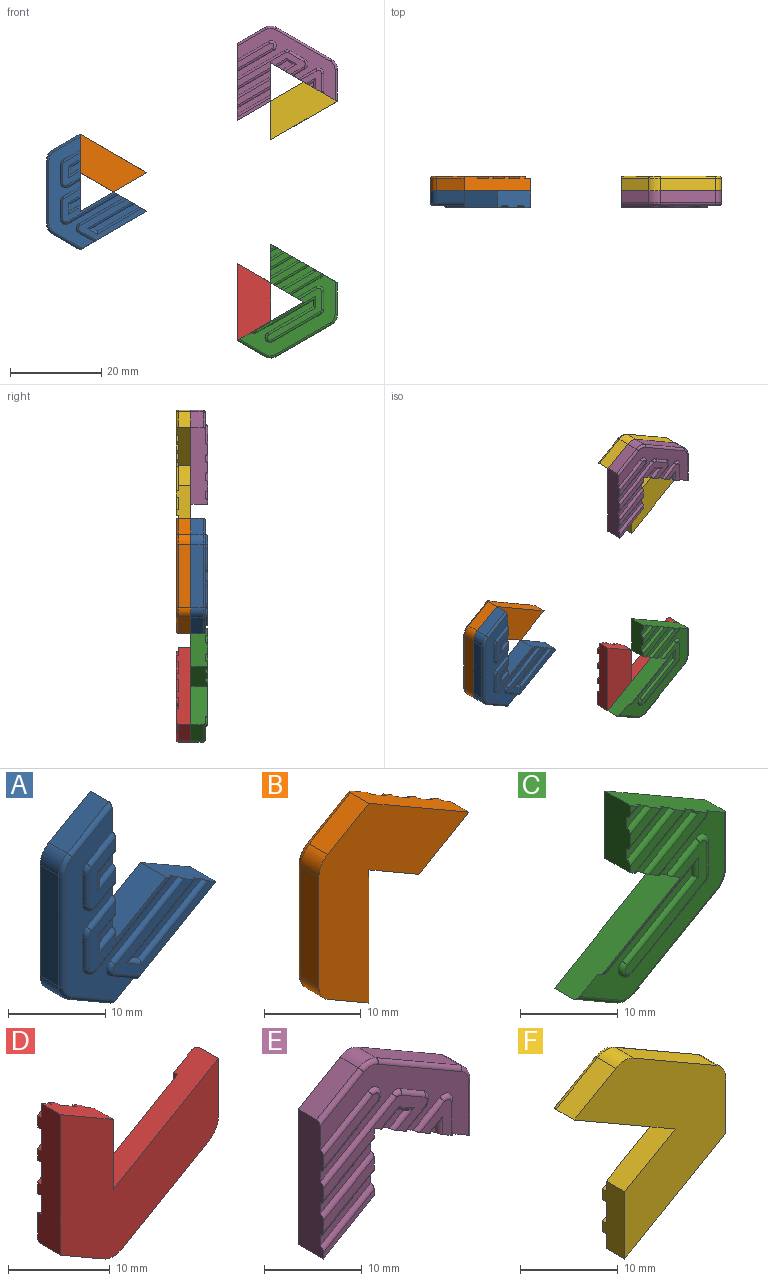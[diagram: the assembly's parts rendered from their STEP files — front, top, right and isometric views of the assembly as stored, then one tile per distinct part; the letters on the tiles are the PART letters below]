
ASSEMBLY  parts=6 mates=14
PART A: 44 faces, bbox 22.1x3.7x25.5 mm
  f0: plane 2.58x2.05mm, normal (0,-1,0), area 2.9mm2, adj f9,f41,f42,f43
  f1: plane 24.46x16.39mm, normal (0,-1,0), area 98.9mm2, adj f6,f7,f9,f17,f18,f19,f20,f21
  f2: plane 2.58x2.05mm, normal (0,-1,0), area 2.9mm2, adj f9,f38,f39,f40
  f3: plane 10.5x6.06mm, normal (0,-1,0), area 12.9mm2, adj f7,f35,f36,f37
  f4: cylinder r=2.54mm len=2.68mm, axis (0,1,0), area 7.1mm2, adj f5,f12,f13,f28
  f5: plane 6.04x3.49mm, normal (-0.5,0,-0.87), area 18.7mm2, adj f4,f6,f13,f27
  f6: plane 14.62x8.44mm, normal (0.5,0,-0.87), area 60.2mm2, adj f1,f5,f7,f13,f14,f27,f32
  f7: plane 7.31x4.22mm, normal (0.5,0,0.87), area 29.4mm2, adj f1,f3,f6,f8,f13,f14,f15,f21
  f8: plane 7.31x4.22mm, normal (-0.5,0,0.87), area 31mm2, adj f7,f9,f13,f15
  f9: plane 16.89x3.68mm, normal (1,0,0), area 57.7mm2, adj f0,f1,f2,f8,f10,f13,f15,f16
  f10: plane 6.04x3.49mm, normal (-0.5,0,0.87), area 18.7mm2, adj f9,f11,f13,f31
  f11: cylinder r=2.54mm len=2.68mm, axis (0,1,0), area 7.1mm2, adj f10,f12,f13,f30
  f12: plane 13.95x2.68mm, normal (-1,0,0), area 37.3mm2, adj f4,f11,f13,f29
  f13: plane 25.33x21.94mm, normal (0,1,0), area 246.3mm2, adj f4,f5,f6,f7,f8,f9,f10,f11
  f14: plane 14.97x9mm, normal (0,-1,0), area 32.7mm2, adj f6,f7,f32,f33,f34,f35,f36,f37
  f15: plane 11.68x7.18mm, normal (0,-1,0), area 18.9mm2, adj f7,f8,f9,f17,f18,f19,f20,f21
  f16: plane 7.18x3.8mm, normal (0,-1,0), area 13.9mm2, adj f9,f22,f23,f24,f25,f26,f41,f42
  f17: cylinder r=0.5mm len=3.99mm, axis (0.87,0,0.5), area 3.3mm2, adj f1,f9,f15,f18
  f18: torus R=0.63mm, axis (0,-1,0), area 0.8mm2, adj f1,f15,f17,f19
  f19: cylinder r=0.5mm len=4mm, axis (0,0,1), area 3.1mm2, adj f1,f15,f18,f20
  f20: torus R=0.63mm, axis (0,-1,0), area 1.6mm2, adj f1,f15,f19,f21
  f21: cylinder r=0.5mm len=11.24mm, axis (-0.87,0,-0.5), area 9.9mm2, adj f1,f7,f15,f20
  f22: cylinder r=0.5mm len=3.99mm, axis (0.87,0,0.5), area 3.3mm2, adj f1,f9,f16,f23
  f23: torus R=0.63mm, axis (0,-1,0), area 0.8mm2, adj f1,f16,f22,f24
  f24: cylinder r=0.5mm len=4mm, axis (0,0,1), area 3.1mm2, adj f1,f16,f23,f25
  f25: torus R=0.63mm, axis (0,-1,0), area 1.6mm2, adj f1,f16,f24,f26
  f26: cylinder r=0.5mm len=3.11mm, axis (-0.87,0,-0.5), area 2.5mm2, adj f1,f9,f16,f25
  f27: cylinder r=0.5mm len=6.54mm, axis (-0.87,0,0.5), area 5.6mm2, adj f1,f5,f6,f28
  f28: torus R=2.04mm, axis (0,-1,0), area 1.9mm2, adj f1,f4,f27,f29
  f29: cylinder r=0.5mm len=13.95mm, axis (0,0,1), area 11mm2, adj f1,f12,f28,f30
  f30: torus R=2.04mm, axis (0,-1,0), area 1.9mm2, adj f1,f11,f29,f31
  f31: cylinder r=0.5mm len=6.29mm, axis (0.87,0,0.5), area 5.4mm2, adj f1,f9,f10,f30
  f32: cylinder r=0.5mm len=3.86mm, axis (-0.87,0,0.5), area 3.1mm2, adj f1,f6,f14,f33
  f33: torus R=0.63mm, axis (0,-1,0), area 1.6mm2, adj f1,f14,f32,f34
  f34: cylinder r=0.5mm len=10.36mm, axis (0.87,0,0.5), area 9mm2, adj f1,f7,f14,f33
  f35: cylinder r=0.5mm len=10.3mm, axis (-0.87,0,-0.5), area 8.6mm2, adj f3,f7,f14,f37
  f36: cylinder r=0.5mm len=10.04mm, axis (0.87,0,0.5), area 8.6mm2, adj f3,f7,f14,f37
  f37: cylinder r=0.5mm len=2.46mm, axis (0.87,0,-0.5), area 1.4mm2, adj f3,f14,f35,f36
  f38: cylinder r=0.5mm len=3.05mm, axis (0.87,0,0.5), area 2mm2, adj f2,f9,f15,f39
  f39: cylinder r=0.5mm len=2.55mm, axis (0,0,-1), area 1.4mm2, adj f2,f15,f38,f40
  f40: cylinder r=0.5mm len=2.8mm, axis (-0.87,0,-0.5), area 2mm2, adj f2,f9,f15,f39
  f41: cylinder r=0.5mm len=2.8mm, axis (-0.87,0,-0.5), area 2mm2, adj f0,f9,f16,f43
  f42: cylinder r=0.5mm len=3.05mm, axis (0.87,0,0.5), area 2mm2, adj f0,f9,f16,f43
  f43: cylinder r=0.5mm len=2.55mm, axis (0,0,-1), area 1.4mm2, adj f0,f16,f41,f42
PART B: 48 faces, bbox 22.1x3.2x25.5 mm
  f0: plane 7.31x4.22mm, normal (0.5,0,-0.87), area 22.6mm2, adj f6,f13,f14,f38
  f1: plane 24.46x9.86mm, normal (0,1,0), area 86.3mm2, adj f6,f12,f16,f17,f18,f22,f23,f24
  f2: plane 8.52x4.92mm, normal (0,1,0), area 10.2mm2, adj f6,f13,f29,f41
  f3: plane 8.56x5.64mm, normal (0,1,0), area 11.1mm2, adj f6,f27,f31,f32
  f4: plane 8.52x4.92mm, normal (0,1,0), area 10.2mm2, adj f6,f13,f39,f42
  f5: plane 2.58x2.05mm, normal (0,1,0), area 2.9mm2, adj f12,f15,f20,f21
  f6: plane 14.62x8.44mm, normal (0.5,0,0.87), area 49mm2, adj f0,f1,f2,f3,f4,f7,f14,f28
  f7: plane 6.04x3.49mm, normal (-0.5,0,0.87), area 18.7mm2, adj f6,f8,f14,f47
  f8: cylinder r=2.54mm len=2.68mm, axis (0,-1,0), area 7.1mm2, adj f7,f9,f14,f46
  f9: plane 13.95x2.68mm, normal (-1,0,0), area 37.3mm2, adj f8,f10,f14,f45
  f10: cylinder r=2.54mm len=2.68mm, axis (0,-1,0), area 7.1mm2, adj f9,f11,f14,f44
  f11: plane 6.04x3.49mm, normal (-0.5,0,-0.87), area 18.7mm2, adj f10,f12,f14,f43
  f12: plane 16.89x3.18mm, normal (1,0,0), area 49mm2, adj f1,f5,f11,f13,f14,f19,f20,f21
  f13: plane 7.31x4.22mm, normal (-0.5,0,-0.87), area 24mm2, adj f0,f2,f4,f12,f14,f28,f29,f38
  f14: plane 25.33x21.94mm, normal (0,-1,0), area 246.3mm2, adj f0,f6,f7,f8,f9,f10,f11,f12
  f15: plane 1.39x0.5mm, normal (-1,0,0), area 0.7mm2, adj f5,f19,f20,f21
  f16: cylinder r=1.13mm len=0.98mm, axis (0,1,0), area 0.6mm2, adj f1,f17,f19,f22
  f17: plane 4x0.5mm, normal (1,0,0), area 2mm2, adj f1,f16,f18,f19
  f18: cylinder r=1.13mm len=1.69mm, axis (0,1,0), area 1.2mm2, adj f1,f17,f19,f23
  f19: plane 8.26x4.3mm, normal (0,1,0), area 24.6mm2, adj f12,f15,f16,f17,f18,f20,f21,f22
  f20: plane 2.05x1.18mm, normal (0.5,0,-0.87), area 1.2mm2, adj f5,f12,f15,f19
  f21: plane 2.05x1.18mm, normal (-0.5,0,0.87), area 1.2mm2, adj f5,f12,f15,f19
  f22: plane 3.74x2.16mm, normal (0.5,0,-0.87), area 2.2mm2, adj f1,f12,f16,f19
  f23: plane 2.61x1.51mm, normal (-0.5,0,0.87), area 1.5mm2, adj f1,f12,f18,f19
  f24: cylinder r=1.13mm len=0.98mm, axis (0,1,0), area 0.6mm2, adj f1,f25,f28,f33
  f25: plane 4x0.5mm, normal (1,0,0), area 2mm2, adj f1,f24,f26,f28
  f26: cylinder r=1.13mm len=1.69mm, axis (0,1,0), area 1.2mm2, adj f1,f25,f28,f30
  f27: plane 1.39x0.5mm, normal (-1,0,0), area 0.7mm2, adj f3,f28,f31,f32
  f28: plane 13.07x10.02mm, normal (0,1,0), area 54.2mm2, adj f6,f12,f13,f24,f25,f26,f27,f29
  f29: plane 7.32x4.22mm, normal (-0.5,0,0.87), area 4.2mm2, adj f2,f6,f13,f28
  f30: plane 2.61x1.51mm, normal (-0.5,0,0.87), area 1.5mm2, adj f1,f12,f26,f28
  f31: plane 8.56x4.94mm, normal (0.5,0,-0.87), area 4.9mm2, adj f3,f6,f27,f28
  f32: plane 7.35x4.24mm, normal (-0.5,0,0.87), area 4.2mm2, adj f3,f6,f27,f28
  f33: plane 6.79x3.92mm, normal (0.5,0,-0.87), area 3.9mm2, adj f1,f6,f24,f28
  f34: cylinder r=1.13mm len=1.95mm, axis (0,1,0), area 1.2mm2, adj f1,f35,f36,f37
  f35: plane 2.28x0.85mm, normal (0,1,0), area 1.4mm2, adj f12,f34,f36,f37
  f36: plane 0.5x0.28mm, normal (0.5,0,-0.87), area 0.2mm2, adj f1,f12,f34,f35
  f37: plane 0.5x0.28mm, normal (0.5,0,0.87), area 0.2mm2, adj f1,f12,f34,f35
  f38: plane 8.51x4.91mm, normal (0,1,0), area 10.1mm2, adj f0,f6,f13,f39
  f39: plane 7.31x4.22mm, normal (0.5,0,-0.87), area 4.2mm2, adj f4,f6,f13,f38
  f40: plane 9.57x5.52mm, normal (0,1,0), area 19mm2, adj f6,f13,f41,f42
  f41: plane 7.31x4.22mm, normal (0.5,0,-0.87), area 4.2mm2, adj f2,f6,f13,f40
  f42: plane 7.32x4.22mm, normal (-0.5,0,0.87), area 4.2mm2, adj f4,f6,f13,f40
  f43: cylinder r=0.5mm len=6.29mm, axis (-0.87,0,0.5), area 5.4mm2, adj f1,f11,f12,f44
  f44: torus R=2.04mm, axis (0,-1,0), area 1.9mm2, adj f1,f10,f43,f45
  f45: cylinder r=0.5mm len=13.95mm, axis (0,0,1), area 11mm2, adj f1,f9,f44,f46
  f46: torus R=2.04mm, axis (0,-1,0), area 1.9mm2, adj f1,f8,f45,f47
  f47: cylinder r=0.5mm len=6.54mm, axis (0.87,0,0.5), area 5.6mm2, adj f1,f6,f7,f46
PART C: 45 faces, bbox 22.1x3.7x25.1 mm
  f0: plane 2.66x2.23mm, normal (0,-1,0), area 2.9mm2, adj f10,f11,f38,f39
  f1: plane 6.12x4.23mm, normal (0,-1,0), area 7.7mm2, adj f10,f11,f40,f42
  f2: plane 8.3x4.92mm, normal (0,-1,0), area 10.2mm2, adj f10,f12,f41,f43,f44
  f3: plane 20.94x17.76mm, normal (0,-1,0), area 104.9mm2, adj f4,f10,f12,f19,f20,f21,f22,f23
  f4: plane 14.62x8.44mm, normal (-0.5,0,0.87), area 60.2mm2, adj f3,f5,f12,f13,f14,f19,f20,f31
  f5: plane 6.04x3.49mm, normal (-0.5,0,-0.87), area 18.7mm2, adj f4,f6,f13,f31
  f6: cylinder r=2.54mm len=2.68mm, axis (0,1,0), area 7.1mm2, adj f5,f7,f13,f32
  f7: plane 12.08x6.98mm, normal (0.5,0,-0.87), area 37.3mm2, adj f6,f8,f13,f33
  f8: cylinder r=2.54mm len=2.68mm, axis (0,1,0), area 7.1mm2, adj f7,f9,f13,f34
  f9: plane 6.98x2.68mm, normal (1,0,0), area 18.7mm2, adj f8,f10,f13,f35
  f10: plane 14.62x8.44mm, normal (0.5,0,0.87), area 57.8mm2, adj f0,f1,f2,f3,f9,f11,f13,f15
  f11: plane 8.44x3.68mm, normal (-1,0,0), area 29.4mm2, adj f0,f1,f10,f12,f13,f16,f17,f18
  f12: plane 7.31x4.22mm, normal (-0.5,0,-0.87), area 29.4mm2, adj f2,f3,f4,f11,f13,f14,f15,f16
  f13: plane 24.94x21.94mm, normal (0,1,0), area 246.3mm2, adj f4,f5,f6,f7,f8,f9,f10,f11
  f14: plane 14.82x11.36mm, normal (0,-1,0), area 28.2mm2, adj f4,f12,f20,f21,f22,f23,f24,f25
  f15: plane 8.34x5.07mm, normal (0,-1,0), area 10.6mm2, adj f10,f12,f36,f37,f43,f44
  f16: plane 7.87x4.95mm, normal (0,-1,0), area 10.3mm2, adj f10,f11,f12,f41,f42
  f17: plane 4.42x3.27mm, normal (0,-1,0), area 5.5mm2, adj f10,f11,f39,f40
  f18: plane 1.1x0.96mm, normal (0,-1,0), area 0.5mm2, adj f10,f11,f38
  f19: cylinder r=0.5mm len=0.42mm, axis (-0.87,0,0.5), area 0mm2, adj f3,f4,f20
  f20: torus R=0.63mm, axis (0,-1,0), area 0.8mm2, adj f3,f4,f14,f19,f21
  f21: cylinder r=0.5mm len=13.35mm, axis (-0.87,0,-0.5), area 11.5mm2, adj f3,f14,f20,f22
  f22: cylinder r=0.5mm len=2.55mm, axis (0,0,1), area 1.4mm2, adj f3,f14,f21,f23
  f23: cylinder r=0.5mm len=10.53mm, axis (0.87,0,0.5), area 9.2mm2, adj f3,f14,f22,f24
  f24: torus R=0.63mm, axis (0,-1,0), area 1.9mm2, adj f3,f14,f23,f25
  f25: cylinder r=0.5mm len=0.69mm, axis (-0.97,0,-0.26), area 0.4mm2, adj f3,f14,f24,f26
  f26: cylinder r=0.5mm len=10.84mm, axis (-0.87,0,-0.5), area 9.6mm2, adj f3,f14,f25,f27
  f27: torus R=0.63mm, axis (0,-1,0), area 0.8mm2, adj f3,f14,f26,f28
  f28: cylinder r=0.5mm len=4mm, axis (0,0,-1), area 3.1mm2, adj f3,f14,f27,f29
  f29: torus R=0.63mm, axis (0,-1,0), area 1.6mm2, adj f3,f14,f28,f30
  f30: cylinder r=0.5mm len=4.44mm, axis (0.87,0,0.5), area 3.7mm2, adj f3,f12,f14,f29
  f31: cylinder r=0.5mm len=6.29mm, axis (-0.87,0,0.5), area 5.4mm2, adj f3,f4,f5,f32
  f32: torus R=2.04mm, axis (0,-1,0), area 1.9mm2, adj f3,f6,f31,f33
  f33: cylinder r=0.5mm len=12.33mm, axis (-0.87,0,-0.5), area 11mm2, adj f3,f7,f32,f34
  f34: torus R=2.04mm, axis (0,-1,0), area 1.9mm2, adj f3,f8,f33,f35
  f35: cylinder r=0.5mm len=7.27mm, axis (0,0,-1), area 5.6mm2, adj f3,f9,f10,f34
  f36: cylinder r=0.5mm len=7.03mm, axis (-0.87,0,-0.5), area 6mm2, adj f3,f12,f15,f37
  f37: torus R=0.63mm, axis (0,-1,0), area 0.6mm2, adj f3,f10,f15,f36
  f38: cylinder r=0.5mm len=1.71mm, axis (-0.87,0,-0.5), area 1.2mm2, adj f0,f10,f11,f18
  f39: cylinder r=0.5mm len=3.41mm, axis (0.87,0,0.5), area 2.6mm2, adj f0,f10,f11,f17
  f40: cylinder r=0.5mm len=5.17mm, axis (-0.87,0,-0.5), area 4.3mm2, adj f1,f10,f11,f17
  f41: cylinder r=0.5mm len=7.81mm, axis (-0.87,0,-0.5), area 6.6mm2, adj f2,f10,f12,f16
  f42: cylinder r=0.5mm len=6.87mm, axis (0.87,0,0.5), area 5.7mm2, adj f1,f10,f11,f16
  f43: cylinder r=0.5mm len=0.54mm, axis (0,0,1), area 0.2mm2, adj f2,f10,f15,f44
  f44: cylinder r=0.5mm len=7.59mm, axis (0.87,0,0.5), area 6.4mm2, adj f2,f12,f15,f43
PART D: 44 faces, bbox 22.4x3.2x20.9 mm
  f0: plane 14.62x8.44mm, normal (-0.5,0,0.87), area 46.9mm2, adj f5,f12,f13,f14,f25,f30,f43
  f1: plane 7.31x5.62mm, normal (0,1,0), area 10.2mm2, adj f5,f7,f27,f33
  f2: plane 2.66x2.23mm, normal (0,1,0), area 2.9mm2, adj f6,f7,f36,f38
  f3: plane 6.12x4.23mm, normal (0,1,0), area 7.7mm2, adj f6,f7,f32,f35
  f4: plane 4.77x3.45mm, normal (0,1,0), area 5.8mm2, adj f5,f15,f28,f29
  f5: plane 8.44x3.18mm, normal (1,0,0), area 24mm2, adj f0,f1,f4,f6,f14,f25,f27,f28
  f6: plane 7.31x4.22mm, normal (0.5,0,0.87), area 24mm2, adj f2,f3,f5,f7,f14,f31,f32,f34
  f7: plane 16.89x3.18mm, normal (-1,0,0), area 49mm2, adj f1,f2,f3,f6,f8,f13,f14,f25
  f8: plane 6.04x3.49mm, normal (-0.5,0,-0.87), area 18.7mm2, adj f7,f9,f14,f39
  f9: cylinder r=2.54mm len=2.68mm, axis (0,-1,0), area 7.1mm2, adj f8,f10,f14,f40
  f10: plane 12.08x6.98mm, normal (0.5,0,-0.87), area 37.3mm2, adj f9,f11,f14,f41
  f11: cylinder r=2.54mm len=2.68mm, axis (0,-1,0), area 7.1mm2, adj f10,f12,f14,f42
  f12: plane 6.98x2.68mm, normal (1,0,0), area 18.7mm2, adj f0,f11,f14,f43
  f13: plane 21.44x15.7mm, normal (0,1,0), area 95.2mm2, adj f0,f7,f16,f17,f18,f19,f20,f21
  f14: plane 21.94x20.72mm, normal (0,-1,0), area 246.3mm2, adj f0,f5,f6,f7,f8,f9,f10,f11
  f15: plane 1.21x0.69mm, normal (-0.5,0,-0.87), area 0.7mm2, adj f4,f25,f28,f29
  f16: cylinder r=1.13mm len=1.13mm, axis (0,1,0), area 0.6mm2, adj f13,f17,f25,f26
  f17: plane 12.35x7.13mm, normal (-0.5,0,0.87), area 7.1mm2, adj f13,f16,f18,f25
  f18: plane 1.39x0.5mm, normal (1,0,0), area 0.7mm2, adj f13,f17,f19,f25
  f19: plane 10.03x5.79mm, normal (0.5,0,-0.87), area 5.8mm2, adj f13,f18,f20,f25
  f20: cylinder r=1.13mm len=2.1mm, axis (0,1,0), area 1.5mm2, adj f13,f19,f21,f25
  f21: plane 0.56x0.5mm, normal (-0.26,0,0.97), area 0.3mm2, adj f13,f20,f22,f25
  f22: plane 10.59x6.11mm, normal (-0.5,0,0.87), area 6.1mm2, adj f13,f21,f23,f25
  f23: cylinder r=1.13mm len=0.98mm, axis (0,1,0), area 0.6mm2, adj f13,f22,f24,f25
  f24: plane 4x0.5mm, normal (-1,0,0), area 2mm2, adj f13,f23,f25,f30
  f25: plane 18.93x11.36mm, normal (0,1,0), area 78.9mm2, adj f0,f5,f7,f15,f16,f17,f18,f19
  f26: plane 3.19x1.83mm, normal (0.5,0,0.87), area 1.8mm2, adj f7,f13,f16,f25
  f27: plane 7.31x4.22mm, normal (0.5,0,-0.87), area 4.2mm2, adj f1,f5,f7,f25
  f28: plane 3.56x2.05mm, normal (0.5,0,-0.87), area 2.1mm2, adj f4,f5,f15,f25
  f29: plane 4.77x2.75mm, normal (-0.5,0,0.87), area 2.8mm2, adj f4,f5,f15,f25
  f30: cylinder r=1.13mm len=0.5mm, axis (0,1,0), area 0.1mm2, adj f0,f13,f24,f25
  f31: plane 7.31x6.14mm, normal (0,1,0), area 18.2mm2, adj f5,f6,f7,f32,f33
  f32: plane 6.12x3.53mm, normal (0.5,0,-0.87), area 3.5mm2, adj f3,f6,f7,f31
  f33: plane 7.31x4.22mm, normal (-0.5,0,0.87), area 4.2mm2, adj f1,f5,f7,f31
  f34: plane 4.92x4.14mm, normal (0,1,0), area 9.9mm2, adj f6,f7,f35,f36
  f35: plane 4.92x2.84mm, normal (-0.5,0,0.87), area 2.8mm2, adj f3,f6,f7,f34
  f36: plane 2.66x1.53mm, normal (0.5,0,-0.87), area 1.5mm2, adj f2,f6,f7,f34
  f37: plane 1.68x1.45mm, normal (0,1,0), area 1.2mm2, adj f6,f7,f38
  f38: plane 1.45x0.84mm, normal (-0.5,0,0.87), area 0.8mm2, adj f2,f6,f7,f37
  f39: cylinder r=0.5mm len=6.54mm, axis (-0.87,0,0.5), area 5.6mm2, adj f7,f8,f13,f40
  f40: torus R=2.04mm, axis (0,-1,0), area 1.9mm2, adj f9,f13,f39,f41
  f41: cylinder r=0.5mm len=12.33mm, axis (-0.87,0,-0.5), area 11mm2, adj f10,f13,f40,f42
  f42: torus R=2.04mm, axis (0,-1,0), area 1.9mm2, adj f11,f13,f41,f43
  f43: cylinder r=0.5mm len=6.98mm, axis (0,0,-1), area 5.4mm2, adj f0,f12,f13,f42
PART E: 46 faces, bbox 22.4x3.7x20.9 mm
  f0: plane 7.31x5.61mm, normal (0,-1,0), area 10.2mm2, adj f5,f12,f43,f45
  f1: plane 3.32x1.92mm, normal (0,-1,0), area 2.9mm2, adj f6,f40,f41,f42
  f2: plane 7.31x5.61mm, normal (0,-1,0), area 10.2mm2, adj f5,f12,f39,f44
  f3: plane 21.44x15.71mm, normal (0,-1,0), area 96mm2, adj f6,f12,f20,f21,f22,f23,f24,f25
  f4: plane 1.14x0.99mm, normal (0,-1,0), area 0.6mm2, adj f6,f37,f38
  f5: plane 8.44x3.68mm, normal (1,0,0), area 29.4mm2, adj f0,f2,f6,f13,f14,f16,f17,f19
  f6: plane 14.62x8.44mm, normal (-0.5,0,-0.87), area 57.8mm2, adj f1,f3,f4,f5,f7,f14,f15,f17
  f7: plane 6.98x2.68mm, normal (1,0,0), area 18.7mm2, adj f6,f8,f14,f36
  f8: cylinder r=2.54mm len=2.68mm, axis (0,1,0), area 7.1mm2, adj f7,f9,f14,f35
  f9: plane 12.08x6.98mm, normal (0.5,0,0.87), area 37.3mm2, adj f8,f10,f14,f34
  f10: cylinder r=2.54mm len=2.68mm, axis (0,1,0), area 7.1mm2, adj f9,f11,f14,f33
  f11: plane 6.04x3.49mm, normal (-0.5,0,0.87), area 18.7mm2, adj f10,f12,f14,f32
  f12: plane 16.89x3.68mm, normal (-1,0,0), area 57.7mm2, adj f0,f2,f3,f11,f13,f14,f16,f17
  f13: plane 7.31x4.22mm, normal (0.5,0,-0.87), area 31mm2, adj f5,f12,f14,f19
  f14: plane 21.94x20.72mm, normal (0,1,0), area 246.3mm2, adj f5,f6,f7,f8,f9,f10,f11,f12
  f15: plane 4.73x4.5mm, normal (0,-1,0), area 9.1mm2, adj f6,f20,f21,f22,f23,f37,f38
  f16: plane 7.31x5.67mm, normal (0,-1,0), area 10.6mm2, adj f5,f12,f43,f44
  f17: plane 14.97x7.63mm, normal (0,-1,0), area 24.7mm2, adj f5,f6,f12,f27,f28,f29,f30,f31
  f18: plane 8.04x5.63mm, normal (0,-1,0), area 11.4mm2, adj f12,f24,f25,f26
  f19: plane 7.31x5.02mm, normal (0,-1,0), area 5.9mm2, adj f5,f12,f13,f45
  f20: cylinder r=0.5mm len=4.06mm, axis (0.87,0,0.5), area 3.4mm2, adj f3,f6,f15,f21
  f21: torus R=0.63mm, axis (0,-1,0), area 1.6mm2, adj f3,f15,f20,f22
  f22: cylinder r=0.5mm len=4mm, axis (0,0,-1), area 3.1mm2, adj f3,f15,f21,f23
  f23: torus R=0.63mm, axis (0,-1,0), area 0.2mm2, adj f3,f6,f15,f22
  f24: cylinder r=0.5mm len=7.35mm, axis (0.87,0,0.5), area 6.3mm2, adj f3,f12,f18,f25
  f25: torus R=0.63mm, axis (0,-1,0), area 2.3mm2, adj f3,f18,f24,f26
  f26: cylinder r=0.5mm len=8.23mm, axis (-0.87,0,-0.5), area 7.2mm2, adj f3,f12,f18,f25
  f27: cylinder r=0.5mm len=3.18mm, axis (-0.87,0,-0.5), area 2.5mm2, adj f3,f6,f17,f28
  f28: torus R=0.63mm, axis (0,-1,0), area 1.6mm2, adj f3,f17,f27,f29
  f29: cylinder r=0.5mm len=3.71mm, axis (0.87,0,-0.5), area 3.1mm2, adj f3,f17,f28,f30
  f30: torus R=0.63mm, axis (0,-1,0), area 0.8mm2, adj f3,f17,f29,f31
  f31: cylinder r=0.5mm len=10.82mm, axis (0.87,0,0.5), area 9.4mm2, adj f3,f12,f17,f30
  f32: cylinder r=0.5mm len=6.54mm, axis (0.87,0,0.5), area 5.6mm2, adj f3,f11,f12,f33
  f33: torus R=2.04mm, axis (0,-1,0), area 1.9mm2, adj f3,f10,f32,f34
  f34: cylinder r=0.5mm len=12.33mm, axis (0.87,0,-0.5), area 11mm2, adj f3,f9,f33,f35
  f35: torus R=2.04mm, axis (0,-1,0), area 1.9mm2, adj f3,f8,f34,f36
  f36: cylinder r=0.5mm len=6.98mm, axis (0,0,-1), area 5.4mm2, adj f3,f6,f7,f35
  f37: cylinder r=0.5mm len=2.29mm, axis (0,0,1), area 1.2mm2, adj f4,f6,f15,f38
  f38: cylinder r=0.5mm len=2.24mm, axis (-0.87,0,-0.5), area 1.2mm2, adj f4,f6,f15,f37
  f39: cylinder r=0.5mm len=7.81mm, axis (-0.87,0,-0.5), area 6.6mm2, adj f2,f5,f12,f17
  f40: cylinder r=0.5mm len=3.12mm, axis (0.87,0,0.5), area 2.1mm2, adj f1,f6,f17,f41
  f41: cylinder r=0.5mm len=2.46mm, axis (-0.87,0,0.5), area 1.4mm2, adj f1,f17,f40,f42
  f42: cylinder r=0.5mm len=2.87mm, axis (-0.87,0,-0.5), area 2.1mm2, adj f1,f6,f17,f41
  f43: cylinder r=0.5mm len=7.81mm, axis (-0.87,0,-0.5), area 6.6mm2, adj f0,f5,f12,f16
  f44: cylinder r=0.5mm len=7.81mm, axis (0.87,0,0.5), area 6.6mm2, adj f2,f5,f12,f16
  f45: cylinder r=0.5mm len=7.81mm, axis (0.87,0,0.5), area 6.6mm2, adj f0,f5,f12,f19
PART F: 43 faces, bbox 22.1x3.2x25.1 mm
  f0: plane 7.31x4.22mm, normal (-0.5,0,0.87), area 22.6mm2, adj f4,f10,f12,f17
  f1: plane 14.62x8.44mm, normal (0.5,0,-0.87), area 46.9mm2, adj f4,f5,f11,f12,f35,f37,f42
  f2: plane 3.32x1.92mm, normal (0,1,0), area 2.9mm2, adj f10,f22,f29,f30
  f3: plane 9.36x6.8mm, normal (0,1,0), area 13mm2, adj f4,f13,f20,f21
  f4: plane 8.44x3.18mm, normal (-1,0,0), area 24mm2, adj f0,f1,f3,f11,f12,f17,f19,f20
  f5: plane 6.98x2.68mm, normal (1,0,0), area 18.7mm2, adj f1,f6,f12,f42
  f6: cylinder r=2.54mm len=2.68mm, axis (0,-1,0), area 7.1mm2, adj f5,f7,f12,f41
  f7: plane 12.08x6.98mm, normal (0.5,0,0.87), area 37.3mm2, adj f6,f8,f12,f40
  f8: cylinder r=2.54mm len=2.68mm, axis (0,-1,0), area 7.1mm2, adj f7,f9,f12,f39
  f9: plane 6.04x3.49mm, normal (-0.5,0,0.87), area 18.7mm2, adj f8,f10,f12,f38
  f10: plane 14.62x8.44mm, normal (-0.5,0,-0.87), area 49mm2, adj f0,f2,f9,f11,f12,f17,f18,f26
  f11: plane 22.61x20.94mm, normal (0,1,0), area 104.7mm2, adj f1,f4,f10,f14,f15,f16,f18,f19
  f12: plane 24.94x21.94mm, normal (0,-1,0), area 246.3mm2, adj f0,f1,f4,f5,f6,f7,f8,f9
  f13: plane 1.39x0.5mm, normal (1,0,0), area 0.7mm2, adj f3,f17,f20,f21
  f14: cylinder r=1.13mm len=0.98mm, axis (0,1,0), area 0.6mm2, adj f11,f15,f17,f19
  f15: plane 4x0.5mm, normal (-1,0,0), area 2mm2, adj f11,f14,f16,f17
  f16: cylinder r=1.13mm len=1.69mm, axis (0,1,0), area 1.2mm2, adj f11,f15,f17,f18
  f17: plane 12.48x11.62mm, normal (0,1,0), area 53.5mm2, adj f0,f4,f10,f13,f14,f15,f16,f18
  f18: plane 3.81x2.2mm, normal (0.5,0,-0.87), area 2.2mm2, adj f10,f11,f16,f17
  f19: plane 11.05x6.38mm, normal (-0.5,0,0.87), area 6.4mm2, adj f4,f11,f14,f17
  f20: plane 9.36x5.41mm, normal (-0.5,0,0.87), area 5.4mm2, adj f3,f4,f13,f17
  f21: plane 9.36x5.41mm, normal (0.5,0,-0.87), area 5.4mm2, adj f3,f4,f13,f17
  f22: plane 1.21x0.7mm, normal (0.5,0,0.87), area 0.7mm2, adj f2,f26,f29,f30
  f23: cylinder r=1.13mm len=1.95mm, axis (0,1,0), area 1.2mm2, adj f11,f24,f26,f27
  f24: plane 3.46x2mm, normal (-0.5,0,-0.87), area 2mm2, adj f11,f23,f25,f26
  f25: cylinder r=1.13mm len=1.13mm, axis (0,1,0), area 0.6mm2, adj f11,f24,f26,f28
  f26: plane 8.96x5.65mm, normal (0,1,0), area 25mm2, adj f10,f22,f23,f24,f25,f27,f28,f29
  f27: plane 2.68x1.55mm, normal (-0.5,0,0.87), area 1.5mm2, adj f10,f11,f23,f26
  f28: plane 3.81x2.2mm, normal (0.5,0,-0.87), area 2.2mm2, adj f10,f11,f25,f26
  f29: plane 2.12x1.22mm, normal (-0.5,0,0.87), area 1.2mm2, adj f2,f10,f22,f26
  f30: plane 2.12x1.22mm, normal (0.5,0,-0.87), area 1.2mm2, adj f2,f10,f22,f26
  f31: cylinder r=1.13mm len=2.1mm, axis (0,1,0), area 1.8mm2, adj f11,f32,f33,f34
  f32: plane 5.5x3.65mm, normal (0,1,0), area 10.4mm2, adj f10,f31,f33,f34
  f33: plane 2.68x1.55mm, normal (-0.5,0,0.87), area 1.5mm2, adj f10,f11,f31,f32
  f34: plane 3.81x2.2mm, normal (0.5,0,-0.87), area 2.2mm2, adj f10,f11,f31,f32
  f35: plane 11.61x7.71mm, normal (0,1,0), area 20.3mm2, adj f1,f4,f36,f37
  f36: plane 9.93x5.73mm, normal (0.5,0,-0.87), area 5.7mm2, adj f4,f11,f35,f37
  f37: cylinder r=1.13mm len=1.68mm, axis (0,1,0), area 1.1mm2, adj f1,f11,f35,f36
  f38: cylinder r=0.5mm len=6.29mm, axis (0.87,0,0.5), area 5.4mm2, adj f9,f10,f11,f39
  f39: torus R=2.04mm, axis (0,-1,0), area 1.9mm2, adj f8,f11,f38,f40
  f40: cylinder r=0.5mm len=12.33mm, axis (0.87,0,-0.5), area 11mm2, adj f7,f11,f39,f41
  f41: torus R=2.04mm, axis (0,-1,0), area 1.9mm2, adj f6,f11,f40,f42
  f42: cylinder r=0.5mm len=7.27mm, axis (0,0,-1), area 5.6mm2, adj f1,f5,f11,f41
PLACE A t=(-88.12,30.44,2.36)mm
PLACE B t=(-88.12,30.44,2.36)mm
PLACE C t=(-53.67,30.44,-17.53)mm
PLACE D t=(-53.67,30.44,-17.53)mm fixed
PLACE E t=(-53.67,30.44,22.25)mm
PLACE F t=(-53.67,30.44,22.25)mm
MATE planar A.f12 <-> B.f9  axis (-1,0,0) through (-102.75,29.1,2.36)mm
MATE planar A.f5 <-> B.f11  axis (-0.5,0,-0.87) through (-98.46,29.1,-8.56)mm
MATE planar C.f13 <-> A.f13  axis (0,1,0) through (-48.19,30.44,-22.79)mm
MATE planar C.f7 <-> D.f10  axis (0.5,0,-0.87) through (-46.36,29.1,-30.2)mm
MATE planar E.f14 <-> C.f13  axis (0,1,0) through (-51.85,30.44,29.62)mm
MATE planar A.f7 <-> C.f12  axis (0.5,0,0.87) through (-85.85,27.26,1.05)mm
MATE planar E.f7 <-> F.f5  axis (1,0,0) through (-39.04,29.1,25.74)mm
MATE planar D.f14 <-> C.f13  axis (0,-1,0) through (-51.86,30.44,-24.91)mm
MATE planar D.f12 <-> C.f9  axis (1,0,0) through (-39.04,31.78,-21.02)mm
MATE planar E.f14 <-> F.f12  axis (0,1,0) through (-39.04,30.44,29.23)mm
MATE planar E.f9 <-> F.f7  axis (0.5,0,0.87) through (-46.36,29.1,34.91)mm
MATE planar A.f13 <-> B.f14  axis (0,1,0) through (-95.41,30.44,0.24)mm
MATE planar D.f7 <-> E.f12  axis (-1,0,0) through (-60.98,31.9,-21.9)mm
MATE planar A.f6 <-> F.f1  axis (0.5,0,-0.87) through (-80.81,28.6,-1.86)mm
